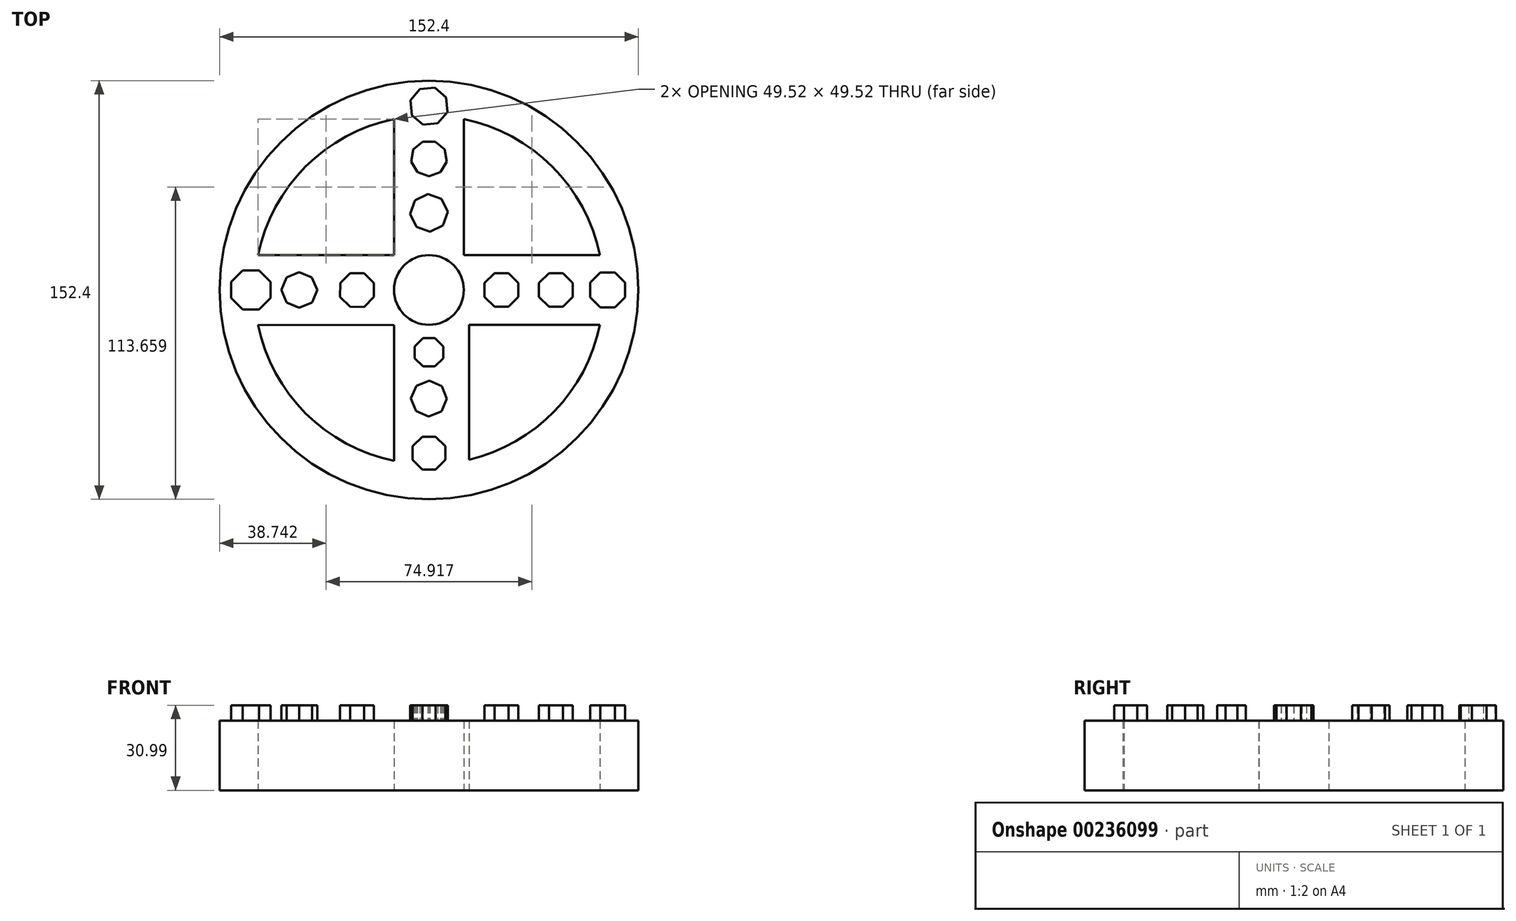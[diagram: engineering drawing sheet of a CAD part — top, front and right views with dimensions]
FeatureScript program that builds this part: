
annotation { "Feature Type Name" : "Feature", "Feature Type Description" : "" }
export const myFeature = defineFeature(function(context is Context, id is Id, definition is map)
    precondition{}
    {
        {
            var Q0;
            Q0=qCreatedBy(makeId("Top.planeOp"),FACE);
            var sketch = newSketch(context, id + "F0", { "sketchPlane" : qUnion([Q0])});
            skCircle(sketch, "E0", {"center": v(0, 0) * mm, "radius": 76.2 * mm});
            skArc(sketch, "E1", {"start": v(-62.22, -12.7) * mm, "mid": v(-44.9, -44.9) * mm, "end": v(-12.7, -62.22) * mm});
            skCircle(sketch, "E2", {"center": v(0, 0) * mm, "radius": 12.7 * mm});
            skLineSegment(sketch, "E3", {"start": v(0, 63.5) * mm, "end": v(0, 0) * mm});
            skLineSegment(sketch, "E4.0", {"start": v(12.7, 76.2) * mm, "end": v(12.7, 75.13) * mm});
            skLineSegment(sketch, "E5.0", {"start": v(-12.7, 76.2) * mm, "end": v(-12.7, 75.13) * mm});
            skLineSegment(sketch, "E6", {"start": v(-63.5, 0) * mm, "end": v(0, 0) * mm});
            skLineSegment(sketch, "E7", {"start": v(63.5, 0) * mm, "end": v(0, 0) * mm});
            skLineSegment(sketch, "E8.0", {"start": v(76.2, 12.7) * mm, "end": v(75.13, 12.7) * mm});
            skLineSegment(sketch, "E9.0", {"start": v(76.2, -12.7) * mm, "end": v(75.13, -12.7) * mm});
            skLineSegment(sketch, "E10.0", {"start": v(-76.2, 12.7) * mm, "end": v(-75.13, 12.7) * mm});
            skLineSegment(sketch, "E11.0", {"start": v(-76.2, -12.7) * mm, "end": v(-75.13, -12.7) * mm});
            skPoint(sketch, "E12.orphan", {"position": v(12.7, 0) * mm});
            skLineSegment(sketch, "E13.trimOffspring", {"start": v(-62.22, 12.7) * mm, "end": v(-12.7, 12.7) * mm});
            skPoint(sketch, "E14.orphan", {"position": v(-76.2, 0) * mm});
            skLineSegment(sketch, "E15.trimOffspring", {"start": v(-12.7, 62.22) * mm, "end": v(-12.7, 12.7) * mm});
            skLineSegment(sketch, "E16.trimOffspring", {"start": v(12.7, 62.22) * mm, "end": v(12.7, 12.7) * mm});
            skLineSegment(sketch, "E17.trimOffspring", {"start": v(62.22, 12.7) * mm, "end": v(12.7, 12.7) * mm});
            skLineSegment(sketch, "E18.trimOffspring", {"start": v(62.22, -12.7) * mm, "end": v(14.67, -12.7) * mm});
            skPoint(sketch, "E19.orphan", {"position": v(76.2, 0) * mm});
            skLineSegment(sketch, "E20.trimOffspring", {"start": v(-12.7, -12.82) * mm, "end": v(-12.7, -62.33) * mm});
            skLineSegment(sketch, "E21.trimOffspring", {"start": v(14.67, -12.62) * mm, "end": v(14.67, -62.14) * mm});
            skArc(sketch, "E22.trimOffspring", {"start": v(14.67, -61.78) * mm, "mid": v(45.61, -44.18) * mm, "end": v(62.22, -12.7) * mm});
            skLineSegment(sketch, "E23", {"start": v(-62.22, -12.7) * mm, "end": v(-12.7, -12.82) * mm});
            skPoint(sketch, "E24.orphan", {"position": v(0, 76.2) * mm});
            skArc(sketch, "E25.trimOffspring", {"start": v(-12.7, 62.22) * mm, "mid": v(-44.9, 44.9) * mm, "end": v(-62.22, 12.7) * mm});
            skArc(sketch, "E26.trimOffspring", {"start": v(62.22, 12.7) * mm, "mid": v(44.9, 44.9) * mm, "end": v(12.7, 62.22) * mm});
            skSolve(sketch);
        }
        {
            var Q0;
            Q0 = qSketchRegion(id + "F0", true);
            extrude(context, id + "F1", {"entities" : qUnion([Q0]), "endBound" : BoundingType.SYMMETRIC, "depth" : 25.4 * mm});
        }
        {
            var Q0;
            Q0=makeQuery(id+"F1.opExtrude","CAP_FACE",FACE,{"disambiguationData":[OSD([sQuery(id+"F0.wireOp",EDGE,"E0"),sQuery(id+"F0.wireOp",EDGE,"E1"),sQuery(id+"F0.wireOp",EDGE,"E2"),sQuery(id+"F0.wireOp",EDGE,"E13.trimOffspring"),sQuery(id+"F0.wireOp",EDGE,"E15.trimOffspring"),sQuery(id+"F0.wireOp",EDGE,"E16.trimOffspring"),sQuery(id+"F0.wireOp",EDGE,"E17.trimOffspring"),sQuery(id+"F0.wireOp",EDGE,"E18.trimOffspring"),sQuery(id+"F0.wireOp",EDGE,"E20.trimOffspring"),sQuery(id+"F0.wireOp",EDGE,"E21.trimOffspring"),sQuery(id+"F0.wireOp",EDGE,"E22.trimOffspring"),sQuery(id+"F0.wireOp",EDGE,"E23"),sQuery(id+"F0.wireOp",EDGE,"E25.trimOffspring"),sQuery(id+"F0.wireOp",EDGE,"E26.trimOffspring")])],"isStart":false});
            var sketch = newSketch(context, id + "F2", { "sketchPlane" : qUnion([Q0])});
            skCircle(sketch, "E27.cCircle", {"center": v(0, 66.92) * mm, "radius": 6.47 * mm, "construction": true});
            skLineSegment(sketch, "E27.0", {"start": v(6.68, 64.81) * mm, "end": v(3.23, 60.7) * mm});
            skLineSegment(sketch, "E27.1", {"start": v(3.23, 60.7) * mm, "end": v(-2.11, 60.24) * mm});
            skLineSegment(sketch, "E27.2", {"start": v(-2.11, 60.24) * mm, "end": v(-6.22, 63.7) * mm});
            skLineSegment(sketch, "E27.3", {"start": v(-6.22, 63.7) * mm, "end": v(-6.68, 69.03) * mm});
            skLineSegment(sketch, "E27.4", {"start": v(-6.68, 69.03) * mm, "end": v(-3.23, 73.14) * mm});
            skLineSegment(sketch, "E27.5", {"start": v(-3.23, 73.14) * mm, "end": v(2.11, 73.6) * mm});
            skLineSegment(sketch, "E27.6", {"start": v(2.11, 73.6) * mm, "end": v(6.22, 70.16) * mm});
            skLineSegment(sketch, "E27.7", {"start": v(6.22, 70.16) * mm, "end": v(6.68, 64.81) * mm});
            skPoint(sketch, "E27.0.midPoint", {"position": v(4.96, 62.76) * mm});
            skCircle(sketch, "E28.cCircle", {"center": v(0, 47.89) * mm, "radius": 6.15 * mm, "construction": true});
            skLineSegment(sketch, "E28.0", {"start": v(-2.24, 54.03) * mm, "end": v(2.24, 54.03) * mm});
            skLineSegment(sketch, "E28.1", {"start": v(2.24, 54.03) * mm, "end": v(5.67, 51.16) * mm});
            skLineSegment(sketch, "E28.2", {"start": v(5.67, 51.16) * mm, "end": v(6.44, 46.75) * mm});
            skLineSegment(sketch, "E28.3", {"start": v(6.44, 46.75) * mm, "end": v(4.2, 42.88) * mm});
            skLineSegment(sketch, "E28.4", {"start": v(4.2, 42.88) * mm, "end": v(0, 41.35) * mm});
            skLineSegment(sketch, "E28.5", {"start": v(0, 41.35) * mm, "end": v(-4.2, 42.88) * mm});
            skLineSegment(sketch, "E28.6", {"start": v(-4.2, 42.88) * mm, "end": v(-6.44, 46.75) * mm});
            skLineSegment(sketch, "E28.7", {"start": v(-6.44, 46.75) * mm, "end": v(-5.67, 51.16) * mm});
            skLineSegment(sketch, "E28.8", {"start": v(-5.67, 51.16) * mm, "end": v(-2.24, 54.03) * mm});
            skPoint(sketch, "E28.0.midPoint", {"position": v(0, 54.03) * mm});
            skCircle(sketch, "E29.cCircle", {"center": v(0, 28.06) * mm, "radius": 6.31 * mm, "construction": true});
            skLineSegment(sketch, "E29.0", {"start": v(-0.35, 34.88) * mm, "end": v(4.57, 33.13) * mm});
            skLineSegment(sketch, "E29.1", {"start": v(4.57, 33.13) * mm, "end": v(6.82, 28.41) * mm});
            skLineSegment(sketch, "E29.2", {"start": v(6.82, 28.41) * mm, "end": v(5.07, 23.48) * mm});
            skLineSegment(sketch, "E29.3", {"start": v(5.07, 23.48) * mm, "end": v(0.35, 21.24) * mm});
            skLineSegment(sketch, "E29.4", {"start": v(0.35, 21.24) * mm, "end": v(-4.57, 22.98) * mm});
            skLineSegment(sketch, "E29.5", {"start": v(-4.57, 22.98) * mm, "end": v(-6.82, 27.7) * mm});
            skLineSegment(sketch, "E29.6", {"start": v(-6.82, 27.7) * mm, "end": v(-5.07, 32.63) * mm});
            skLineSegment(sketch, "E29.7", {"start": v(-5.07, 32.63) * mm, "end": v(-0.35, 34.88) * mm});
            skPoint(sketch, "E29.0.midPoint", {"position": v(2.11, 34) * mm});
            skCircle(sketch, "E30.cCircle", {"center": v(-64.84, 0) * mm, "radius": 7.14 * mm, "construction": true});
            skLineSegment(sketch, "E30.0", {"start": v(-57.7, 2.96) * mm, "end": v(-57.7, -2.96) * mm});
            skLineSegment(sketch, "E30.1", {"start": v(-57.7, -2.96) * mm, "end": v(-61.88, -7.14) * mm});
            skLineSegment(sketch, "E30.2", {"start": v(-61.88, -7.14) * mm, "end": v(-67.8, -7.14) * mm});
            skLineSegment(sketch, "E30.3", {"start": v(-67.8, -7.14) * mm, "end": v(-71.98, -2.96) * mm});
            skLineSegment(sketch, "E30.4", {"start": v(-71.98, -2.96) * mm, "end": v(-71.98, 2.96) * mm});
            skLineSegment(sketch, "E30.5", {"start": v(-71.98, 2.96) * mm, "end": v(-67.8, 7.14) * mm});
            skLineSegment(sketch, "E30.6", {"start": v(-67.8, 7.14) * mm, "end": v(-61.88, 7.14) * mm});
            skLineSegment(sketch, "E30.7", {"start": v(-61.88, 7.14) * mm, "end": v(-57.7, 2.96) * mm});
            skPoint(sketch, "E30.0.midPoint", {"position": v(-57.7, 0) * mm});
            skCircle(sketch, "E31.cCircle", {"center": v(-47.2, 0) * mm, "radius": 6 * mm, "construction": true});
            skLineSegment(sketch, "E31.0", {"start": v(-53.69, -0.02) * mm, "end": v(-51.8, 4.58) * mm});
            skLineSegment(sketch, "E31.1", {"start": v(-51.8, 4.58) * mm, "end": v(-47.21, 6.5) * mm});
            skLineSegment(sketch, "E31.2", {"start": v(-47.21, 6.5) * mm, "end": v(-42.61, 4.6) * mm});
            skLineSegment(sketch, "E31.3", {"start": v(-42.61, 4.6) * mm, "end": v(-40.7, 0.02) * mm});
            skLineSegment(sketch, "E31.4", {"start": v(-40.7, 0.02) * mm, "end": v(-42.59, -4.58) * mm});
            skLineSegment(sketch, "E31.5", {"start": v(-42.59, -4.58) * mm, "end": v(-47.17, -6.5) * mm});
            skLineSegment(sketch, "E31.6", {"start": v(-47.17, -6.5) * mm, "end": v(-51.77, -4.6) * mm});
            skLineSegment(sketch, "E31.7", {"start": v(-51.77, -4.6) * mm, "end": v(-53.69, -0.02) * mm});
            skPoint(sketch, "E31.0.midPoint", {"position": v(-52.75, 2.28) * mm});
            skCircle(sketch, "E32.cCircle", {"center": v(-26.17, 0) * mm, "radius": 6.15 * mm, "construction": true});
            skLineSegment(sketch, "E32.0", {"start": v(-32.33, -2.53) * mm, "end": v(-32.31, 2.57) * mm});
            skLineSegment(sketch, "E32.1", {"start": v(-32.31, 2.57) * mm, "end": v(-28.7, 6.16) * mm});
            skLineSegment(sketch, "E32.2", {"start": v(-28.7, 6.16) * mm, "end": v(-23.6, 6.14) * mm});
            skLineSegment(sketch, "E32.3", {"start": v(-23.6, 6.14) * mm, "end": v(-20.02, 2.53) * mm});
            skLineSegment(sketch, "E32.4", {"start": v(-20.02, 2.53) * mm, "end": v(-20.04, -2.57) * mm});
            skLineSegment(sketch, "E32.5", {"start": v(-20.04, -2.57) * mm, "end": v(-23.65, -6.16) * mm});
            skLineSegment(sketch, "E32.6", {"start": v(-23.65, -6.16) * mm, "end": v(-28.74, -6.14) * mm});
            skLineSegment(sketch, "E32.7", {"start": v(-28.74, -6.14) * mm, "end": v(-32.33, -2.53) * mm});
            skPoint(sketch, "E32.0.midPoint", {"position": v(-32.32, 0.02) * mm});
            skCircle(sketch, "E33.cCircle", {"center": v(65.04, 0) * mm, "radius": 6.35 * mm, "construction": true});
            skLineSegment(sketch, "E33.0", {"start": v(58.7, -2.63) * mm, "end": v(58.7, 2.63) * mm});
            skLineSegment(sketch, "E33.1", {"start": v(58.7, 2.63) * mm, "end": v(62.41, 6.35) * mm});
            skLineSegment(sketch, "E33.2", {"start": v(62.41, 6.35) * mm, "end": v(67.67, 6.35) * mm});
            skLineSegment(sketch, "E33.3", {"start": v(67.67, 6.35) * mm, "end": v(71.38, 2.63) * mm});
            skLineSegment(sketch, "E33.4", {"start": v(71.38, 2.63) * mm, "end": v(71.38, -2.63) * mm});
            skLineSegment(sketch, "E33.5", {"start": v(71.38, -2.63) * mm, "end": v(67.67, -6.35) * mm});
            skLineSegment(sketch, "E33.6", {"start": v(67.67, -6.35) * mm, "end": v(62.41, -6.35) * mm});
            skLineSegment(sketch, "E33.7", {"start": v(62.41, -6.35) * mm, "end": v(58.7, -2.63) * mm});
            skPoint(sketch, "E33.0.midPoint", {"position": v(58.7, 0) * mm});
            skCircle(sketch, "E34.cCircle", {"center": v(46.2, 0) * mm, "radius": 6.15 * mm, "construction": true});
            skLineSegment(sketch, "E34.0", {"start": v(40.05, -2.55) * mm, "end": v(40.05, 2.55) * mm});
            skLineSegment(sketch, "E34.1", {"start": v(40.05, 2.55) * mm, "end": v(43.66, 6.15) * mm});
            skLineSegment(sketch, "E34.2", {"start": v(43.66, 6.15) * mm, "end": v(48.75, 6.15) * mm});
            skLineSegment(sketch, "E34.3", {"start": v(48.75, 6.15) * mm, "end": v(52.35, 2.55) * mm});
            skLineSegment(sketch, "E34.4", {"start": v(52.35, 2.55) * mm, "end": v(52.35, -2.55) * mm});
            skLineSegment(sketch, "E34.5", {"start": v(52.35, -2.55) * mm, "end": v(48.75, -6.15) * mm});
            skLineSegment(sketch, "E34.6", {"start": v(48.75, -6.15) * mm, "end": v(43.66, -6.15) * mm});
            skLineSegment(sketch, "E34.7", {"start": v(43.66, -6.15) * mm, "end": v(40.05, -2.55) * mm});
            skPoint(sketch, "E34.0.midPoint", {"position": v(40.05, 0) * mm});
            skCircle(sketch, "E35.cCircle", {"center": v(26.37, 0) * mm, "radius": 6.15 * mm, "construction": true});
            skLineSegment(sketch, "E35.0", {"start": v(20.23, -2.55) * mm, "end": v(20.23, 2.55) * mm});
            skLineSegment(sketch, "E35.1", {"start": v(20.23, 2.55) * mm, "end": v(23.83, 6.15) * mm});
            skLineSegment(sketch, "E35.2", {"start": v(23.83, 6.15) * mm, "end": v(28.92, 6.15) * mm});
            skLineSegment(sketch, "E35.3", {"start": v(28.92, 6.15) * mm, "end": v(32.52, 2.55) * mm});
            skLineSegment(sketch, "E35.4", {"start": v(32.52, 2.55) * mm, "end": v(32.52, -2.55) * mm});
            skLineSegment(sketch, "E35.5", {"start": v(32.52, -2.55) * mm, "end": v(28.92, -6.15) * mm});
            skLineSegment(sketch, "E35.6", {"start": v(28.92, -6.15) * mm, "end": v(23.83, -6.15) * mm});
            skLineSegment(sketch, "E35.7", {"start": v(23.83, -6.15) * mm, "end": v(20.23, -2.55) * mm});
            skPoint(sketch, "E35.0.midPoint", {"position": v(20.23, 0) * mm});
            skCircle(sketch, "E36.cCircle", {"center": v(0, -59.39) * mm, "radius": 5.95 * mm, "construction": true});
            skLineSegment(sketch, "E36.0", {"start": v(-5.95, -61.85) * mm, "end": v(-5.95, -56.92) * mm});
            skLineSegment(sketch, "E36.1", {"start": v(-5.95, -56.92) * mm, "end": v(-2.46, -53.44) * mm});
            skLineSegment(sketch, "E36.2", {"start": v(-2.46, -53.44) * mm, "end": v(2.46, -53.44) * mm});
            skLineSegment(sketch, "E36.3", {"start": v(2.46, -53.44) * mm, "end": v(5.95, -56.92) * mm});
            skLineSegment(sketch, "E36.4", {"start": v(5.95, -56.92) * mm, "end": v(5.95, -61.85) * mm});
            skLineSegment(sketch, "E36.5", {"start": v(5.95, -61.85) * mm, "end": v(2.46, -65.34) * mm});
            skLineSegment(sketch, "E36.6", {"start": v(2.46, -65.34) * mm, "end": v(-2.46, -65.34) * mm});
            skLineSegment(sketch, "E36.7", {"start": v(-2.46, -65.34) * mm, "end": v(-5.95, -61.85) * mm});
            skPoint(sketch, "E36.0.midPoint", {"position": v(-5.95, -59.39) * mm});
            skCircle(sketch, "E37.cCircle", {"center": v(0, -39.56) * mm, "radius": 6.04 * mm, "construction": true});
            skLineSegment(sketch, "E37.0", {"start": v(-6.54, -39.48) * mm, "end": v(-4.57, -34.88) * mm});
            skLineSegment(sketch, "E37.1", {"start": v(-4.57, -34.88) * mm, "end": v(0.08, -33.02) * mm});
            skLineSegment(sketch, "E37.2", {"start": v(0.08, -33.02) * mm, "end": v(4.68, -35) * mm});
            skLineSegment(sketch, "E37.3", {"start": v(4.68, -35) * mm, "end": v(6.54, -39.64) * mm});
            skLineSegment(sketch, "E37.4", {"start": v(6.54, -39.64) * mm, "end": v(4.57, -44.24) * mm});
            skLineSegment(sketch, "E37.5", {"start": v(4.57, -44.24) * mm, "end": v(-0.08, -46.1) * mm});
            skLineSegment(sketch, "E37.6", {"start": v(-0.08, -46.1) * mm, "end": v(-4.68, -44.13) * mm});
            skLineSegment(sketch, "E37.7", {"start": v(-4.68, -44.13) * mm, "end": v(-6.54, -39.48) * mm});
            skPoint(sketch, "E37.0.midPoint", {"position": v(-5.55, -37.18) * mm});
            skCircle(sketch, "E38.cCircle", {"center": v(0, -22.7) * mm, "radius": 5.16 * mm, "construction": true});
            skLineSegment(sketch, "E38.0", {"start": v(-5.16, -24.84) * mm, "end": v(-5.16, -20.57) * mm});
            skLineSegment(sketch, "E38.1", {"start": v(-5.16, -20.57) * mm, "end": v(-2.14, -17.55) * mm});
            skLineSegment(sketch, "E38.2", {"start": v(-2.14, -17.55) * mm, "end": v(2.14, -17.55) * mm});
            skLineSegment(sketch, "E38.3", {"start": v(2.14, -17.55) * mm, "end": v(5.16, -20.57) * mm});
            skLineSegment(sketch, "E38.4", {"start": v(5.16, -20.57) * mm, "end": v(5.16, -24.84) * mm});
            skLineSegment(sketch, "E38.5", {"start": v(5.16, -24.84) * mm, "end": v(2.14, -27.86) * mm});
            skLineSegment(sketch, "E38.6", {"start": v(2.14, -27.86) * mm, "end": v(-2.14, -27.86) * mm});
            skLineSegment(sketch, "E38.7", {"start": v(-2.14, -27.86) * mm, "end": v(-5.16, -24.84) * mm});
            skPoint(sketch, "E38.0.midPoint", {"position": v(-5.16, -22.7) * mm});
            skSolve(sketch);
        }
        {
            var Q0;
            Q0=makeQuery(id+"F2.imprint","IMPRINT",FACE,{"disambiguationData":[TD([[makeQuery(id+"F2.imprint","IMPRINT",EDGE,{"derivedFrom":sQuery(id+"F2.wireOp",EDGE,"E27.0")}),-1.0]])]});
            var Q1;
            Q1=makeQuery(id+"F2.imprint","IMPRINT",FACE,{"disambiguationData":[TD([[makeQuery(id+"F2.imprint","IMPRINT",EDGE,{"derivedFrom":sQuery(id+"F2.wireOp",EDGE,"E28.0")}),-1.0]])]});
            var Q2;
            Q2=makeQuery(id+"F2.imprint","IMPRINT",FACE,{"disambiguationData":[TD([[makeQuery(id+"F2.imprint","IMPRINT",EDGE,{"derivedFrom":sQuery(id+"F2.wireOp",EDGE,"E29.0")}),-1.0]])]});
            var Q3;
            Q3=makeQuery(id+"F2.imprint","IMPRINT",FACE,{"disambiguationData":[TD([[makeQuery(id+"F2.imprint","IMPRINT",EDGE,{"derivedFrom":sQuery(id+"F2.wireOp",EDGE,"E30.0")}),-1.0]])]});
            var Q4;
            Q4=makeQuery(id+"F2.imprint","IMPRINT",FACE,{"disambiguationData":[TD([[makeQuery(id+"F2.imprint","IMPRINT",EDGE,{"derivedFrom":sQuery(id+"F2.wireOp",EDGE,"E31.0")}),-1.0]])]});
            var Q5;
            Q5=makeQuery(id+"F2.imprint","IMPRINT",FACE,{"disambiguationData":[TD([[makeQuery(id+"F2.imprint","IMPRINT",EDGE,{"derivedFrom":sQuery(id+"F2.wireOp",EDGE,"E32.0")}),-1.0]])]});
            var Q6;
            Q6=makeQuery(id+"F2.imprint","IMPRINT",FACE,{"disambiguationData":[TD([[makeQuery(id+"F2.imprint","IMPRINT",EDGE,{"derivedFrom":sQuery(id+"F2.wireOp",EDGE,"E38.0")}),-1.0]])]});
            var Q7;
            Q7=makeQuery(id+"F2.imprint","IMPRINT",FACE,{"disambiguationData":[TD([[makeQuery(id+"F2.imprint","IMPRINT",EDGE,{"derivedFrom":sQuery(id+"F2.wireOp",EDGE,"E37.0")}),-1.0]])]});
            var Q8;
            Q8=makeQuery(id+"F2.imprint","IMPRINT",FACE,{"disambiguationData":[TD([[makeQuery(id+"F2.imprint","IMPRINT",EDGE,{"derivedFrom":sQuery(id+"F2.wireOp",EDGE,"E36.0")}),-1.0]])]});
            var Q9;
            Q9=makeQuery(id+"F2.imprint","IMPRINT",FACE,{"disambiguationData":[TD([[makeQuery(id+"F2.imprint","IMPRINT",EDGE,{"derivedFrom":sQuery(id+"F2.wireOp",EDGE,"E35.0")}),-1.0]])]});
            var Q10;
            Q10=makeQuery(id+"F2.imprint","IMPRINT",FACE,{"disambiguationData":[TD([[makeQuery(id+"F2.imprint","IMPRINT",EDGE,{"derivedFrom":sQuery(id+"F2.wireOp",EDGE,"E34.0")}),-1.0]])]});
            var Q11;
            Q11=makeQuery(id+"F2.imprint","IMPRINT",FACE,{"disambiguationData":[TD([[makeQuery(id+"F2.imprint","IMPRINT",EDGE,{"derivedFrom":sQuery(id+"F2.wireOp",EDGE,"E33.0")}),-1.0]])]});
            extrude(context, id + "F3", {"entities" : qUnion([Q0, Q1, Q2, Q3, Q4, Q5, Q6, Q7, Q8, Q9, Q10, Q11]), "operationType" : NewBodyOperationType.ADD, "depth" : 5.6 * mm});
        }
    });
